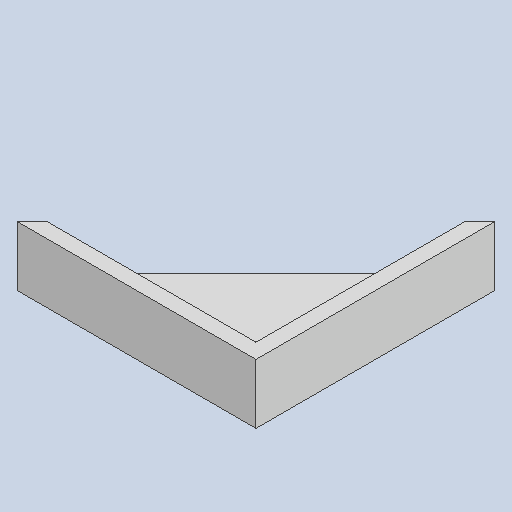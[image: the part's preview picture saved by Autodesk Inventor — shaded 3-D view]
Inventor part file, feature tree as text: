
AUTODESK INVENTOR PART (.ipt)
format: ipt  version: 2023 (Build 270158000, 158)  size: 135,168 bytes
history: native  units: in
note: dims shown in document units (in); Inventor stores cm internally (conversion verified against a paired STEP export)
features: extrude x1, shell x1, sketch x1
ambient origin geometry x8: Origin, YZ Plane, XZ Plane, XY Plane, X Axis, Y Axis, Z Axis, Center Point
bodies: Solid1 (feature_tree)
feature tree (3):
  extrude  "Extrusion1"  Depth=0.5in TaperAngle=0.0deg
  shell  "Shell1"  Thickness=0.125in
  sketch  "Sketch1"  dims[d0=2.0in d1=0.5in d2=0.0in d3=0.125in]
